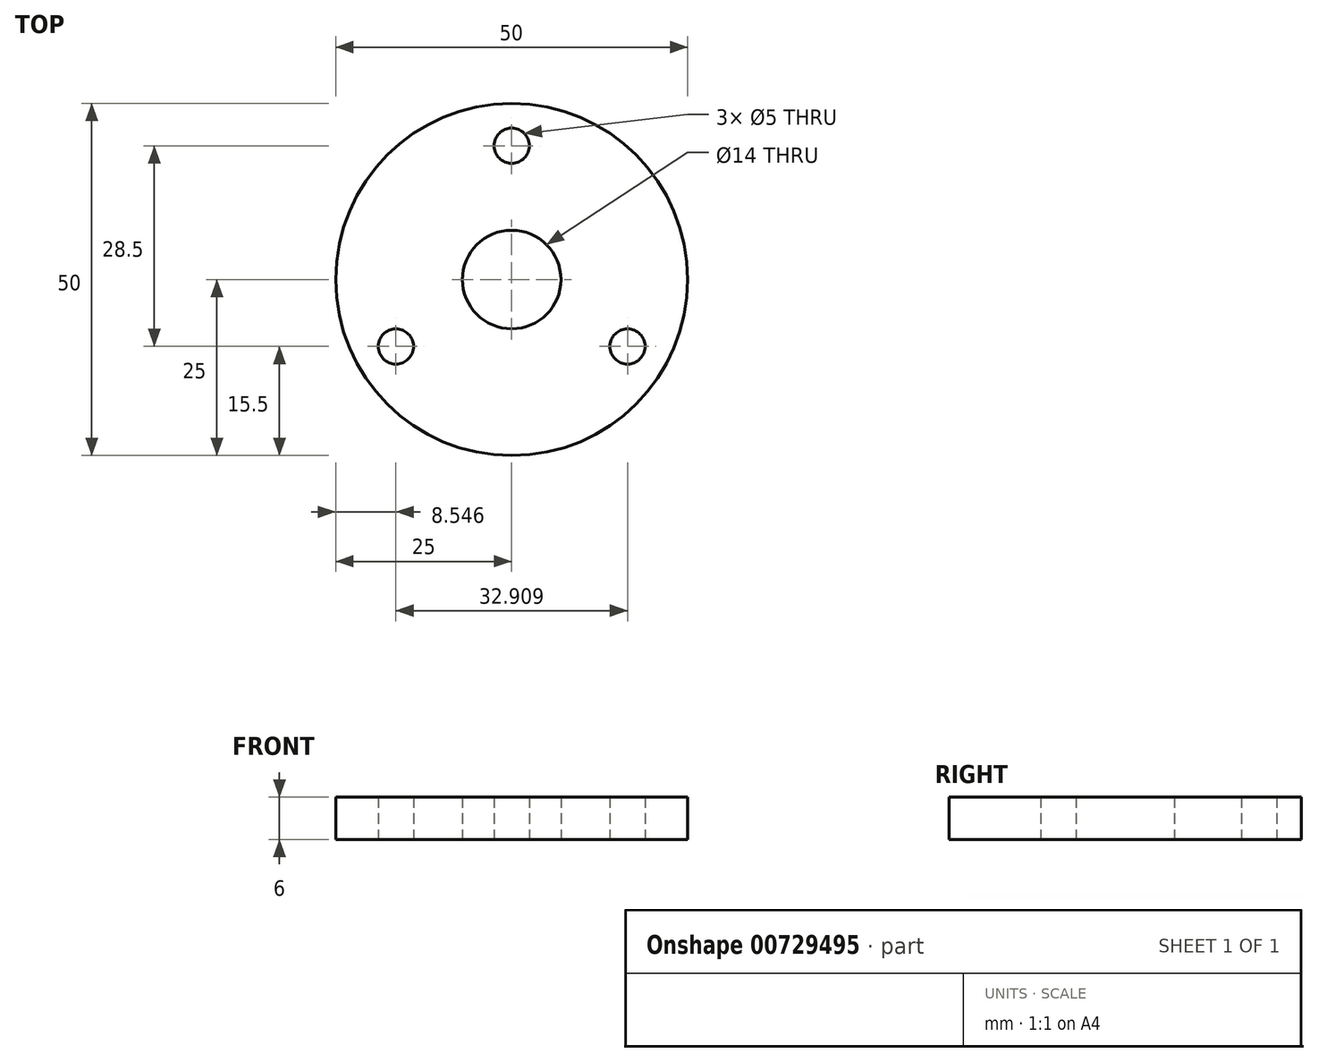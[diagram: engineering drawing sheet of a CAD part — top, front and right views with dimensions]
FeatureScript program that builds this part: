
annotation { "Feature Type Name" : "Feature", "Feature Type Description" : "" }
export const myFeature = defineFeature(function(context is Context, id is Id, definition is map)
    precondition{}
    {
        {
            var Q0;
            Q0=qCreatedBy(makeId("Top.planeOp"),FACE);
            var sketch = newSketch(context, id + "F0", { "sketchPlane" : qUnion([Q0])});
            skCircle(sketch, "E0", {"center": v(0, 0) * mm, "radius": 25 * mm});
            skCircle(sketch, "E1", {"center": v(0, 0) * mm, "radius": 7 * mm});
            skCircle(sketch, "E2", {"center": v(0, 19) * mm, "radius": 2.5 * mm});
            skCircle(sketch, "E3", {"center": v(16.45, -9.5) * mm, "radius": 2.5 * mm});
            skCircle(sketch, "E4", {"center": v(-16.45, -9.5) * mm, "radius": 2.5 * mm});
            skLineSegment(sketch, "E5", {"start": v(0, 0) * mm, "end": v(16.45, -9.5) * mm, "construction": true});
            skLineSegment(sketch, "E6", {"start": v(0, 19) * mm, "end": v(0, 0) * mm, "construction": true});
            skLineSegment(sketch, "E7", {"start": v(0, 0) * mm, "end": v(-16.45, -9.5) * mm, "construction": true});
            skSolve(sketch);
        }
        {
            var Q0;
            Q0=makeQuery(id+"F0.imprint","IMPRINT",FACE,{"disambiguationData":[TD([[makeQuery(id+"F0.imprint","IMPRINT",EDGE,{"derivedFrom":sQuery(id+"F0.wireOp",EDGE,"E0")}),1.0]])]});
            extrude(context, id + "F1", {"entities" : qUnion([Q0]), "depth" : 6 * mm, "offsetDistance" : 25 * mm});
        }
    });
